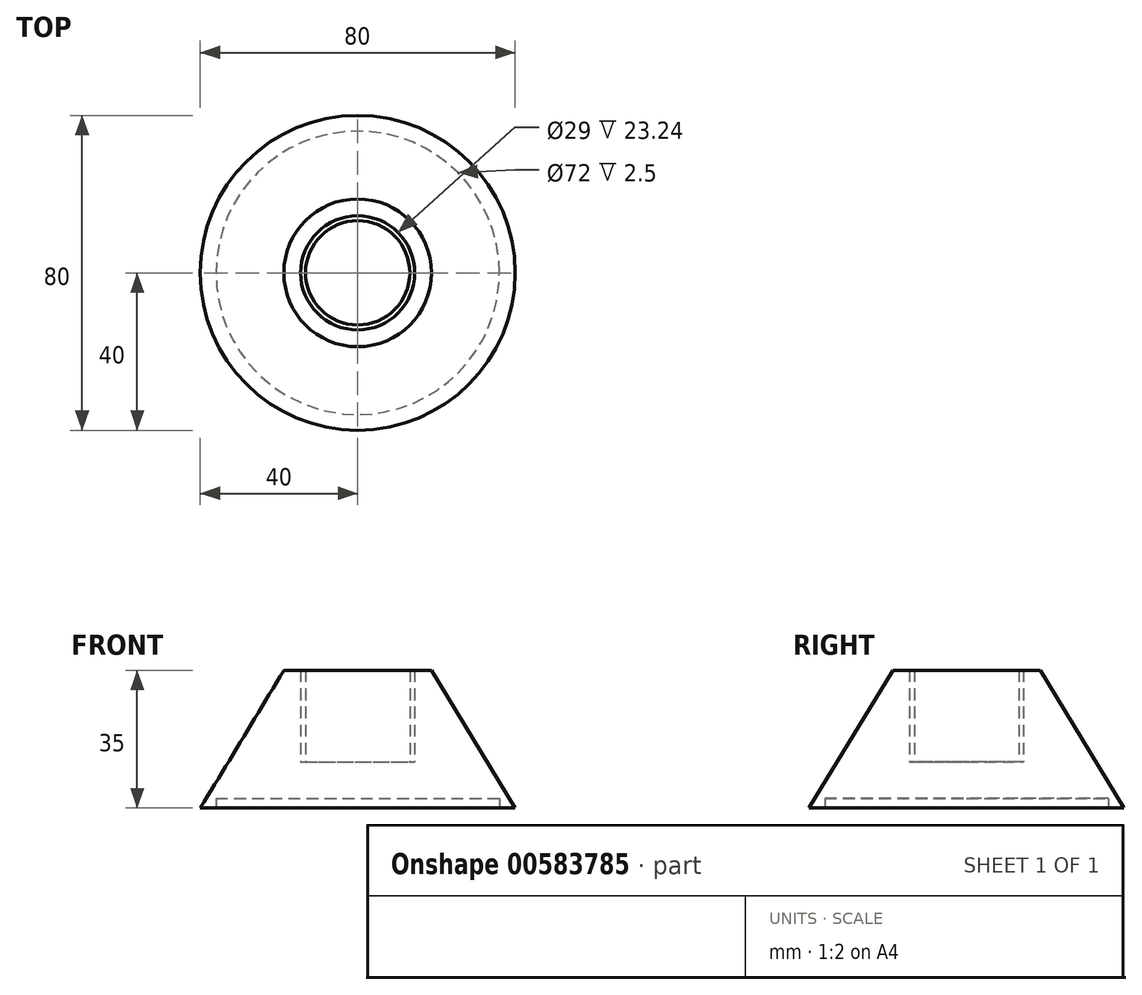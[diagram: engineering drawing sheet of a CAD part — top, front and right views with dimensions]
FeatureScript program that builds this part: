
annotation { "Feature Type Name" : "Feature", "Feature Type Description" : "" }
export const myFeature = defineFeature(function(context is Context, id is Id, definition is map)
    precondition{}
    {
        {
            var Q0;
            Q0=qCreatedBy(makeId("Front.planeOp"),FACE);
            var sketch = newSketch(context, id + "F0", { "sketchPlane" : qUnion([Q0])});
            skLineSegment(sketch, "E0", {"start": v(0, 35) * mm, "end": v(-13.25, 35) * mm});
            skLineSegment(sketch, "E1", {"start": v(-13.25, 35) * mm, "end": v(-13.25, 11.76) * mm});
            skLineSegment(sketch, "E2", {"start": v(-13.25, 11.76) * mm, "end": v(-14.5, 11.76) * mm});
            skLineSegment(sketch, "E3", {"start": v(-14.5, 11.76) * mm, "end": v(-14.5, 35) * mm});
            skLineSegment(sketch, "E4", {"start": v(0, 0) * mm, "end": v(0, 35) * mm});
            skLineSegment(sketch, "E5", {"start": v(-14.5, 35) * mm, "end": v(-18.76, 35) * mm});
            skLineSegment(sketch, "E6", {"start": v(-18.76, 35) * mm, "end": v(-40, 0) * mm});
            skLineSegment(sketch, "E7", {"start": v(-40, 0) * mm, "end": v(-36, 0) * mm});
            skLineSegment(sketch, "E8", {"start": v(-36, 0) * mm, "end": v(-36, 2.5) * mm});
            skLineSegment(sketch, "E9", {"start": v(-36, 2.5) * mm, "end": v(0, 2.5) * mm});
            skSolve(sketch);
        }
        {
            var Q0;
            Q0=makeQuery(id+"F0.imprint","IMPRINT",FACE,{"disambiguationData":[TD([[makeQuery(id+"F0.imprint","IMPRINT",EDGE,{"derivedFrom":sQuery(id+"F0.wireOp",EDGE,"E0")}),1.0]])]});
            var Q1;
            Q1=sQuery(id+"F0.wireOp",EDGE,"E4");
            revolve(context, id + "F1", {"entities" : qUnion([Q0]), "axis" : qUnion([Q1]), "revolveType" : RevolveType.FULL});
        }
    });
